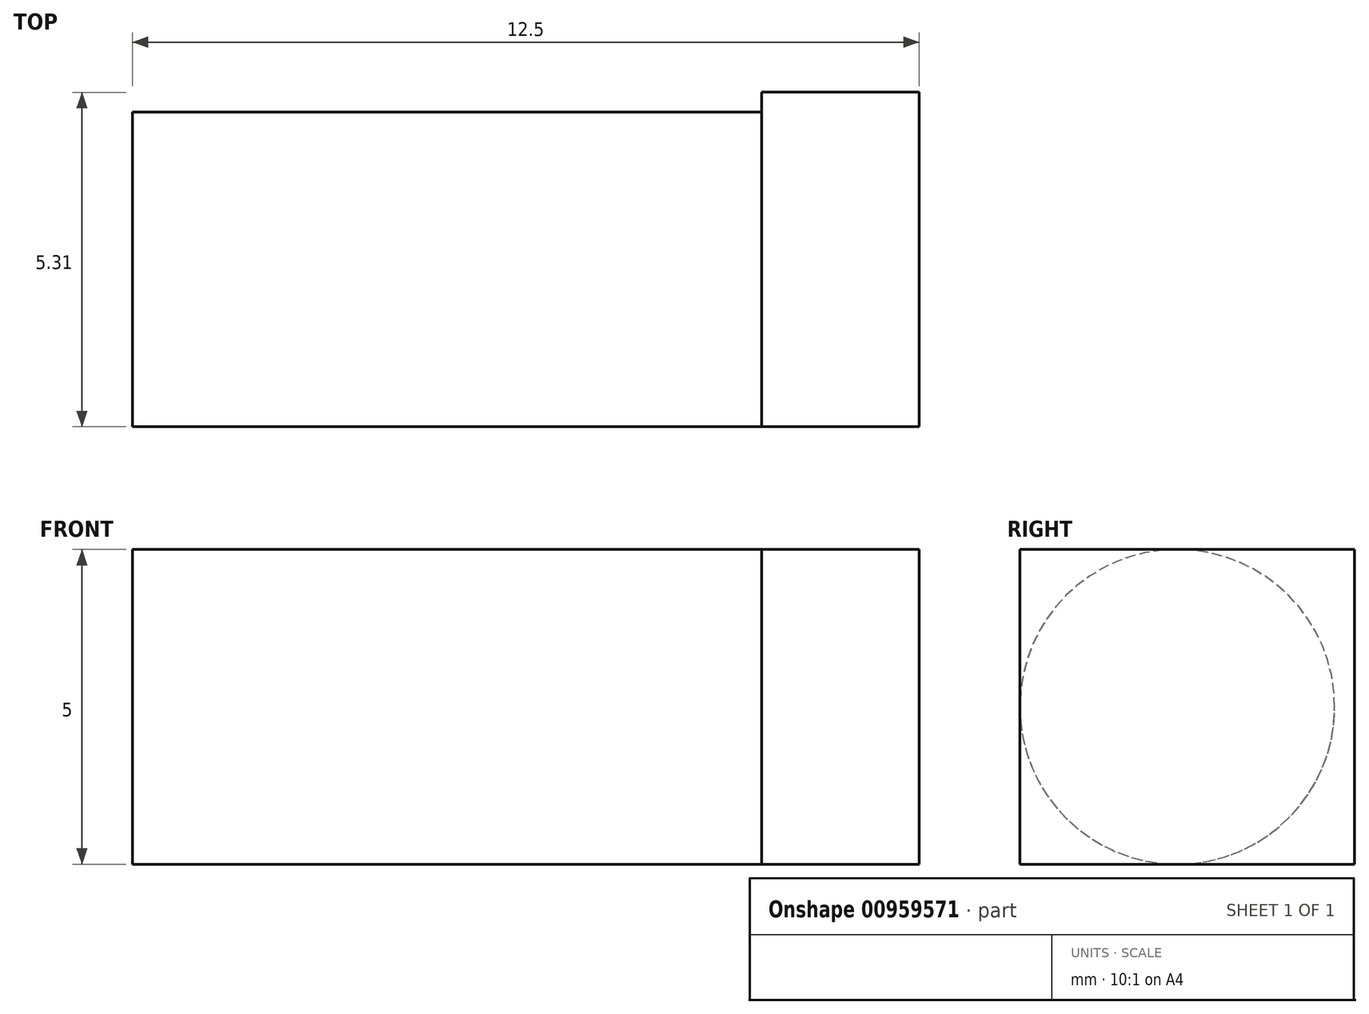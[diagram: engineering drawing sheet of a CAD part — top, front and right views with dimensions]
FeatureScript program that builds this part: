
annotation { "Feature Type Name" : "Feature", "Feature Type Description" : "" }
export const myFeature = defineFeature(function(context is Context, id is Id, definition is map)
    precondition{}
    {
        {
            var Q0;
            Q0=qCreatedBy(makeId("Right.planeOp"),FACE);
            var sketch = newSketch(context, id + "F0", { "sketchPlane" : qUnion([Q0])});
            skCircle(sketch, "E0", {"center": v(0, 0) * mm, "radius": 2.5 * mm});
            skSolve(sketch);
        }
        {
            var Q0;
            Q0=makeQuery(id+"F0.imprint","IMPRINT",FACE,{"disambiguationData":[TD([[makeQuery(id+"F0.imprint","IMPRINT",EDGE,{"derivedFrom":sQuery(id+"F0.wireOp",EDGE,"E0")}),1.0]])]});
            extrude(context, id + "F1", {"entities" : qUnion([Q0]), "depth" : 10 * mm, "offsetDistance" : 25 * mm});
        }
        {
            var Q0;
            Q0=makeQuery(id+"F1.opExtrude","CAP_FACE",FACE,{"disambiguationData":[OSD([sQuery(id+"F0.wireOp",EDGE,"E0")])],"isStart":false});
            var sketch = newSketch(context, id + "F2", { "sketchPlane" : qUnion([Q0])});
            skLineSegment(sketch, "E1", {"start": v(-2.5, 0) * mm, "end": v(-2.5, 2.5) * mm});
            skLineSegment(sketch, "E2.bottom", {"start": v(-2.5, 2.5) * mm, "end": v(2.81, 2.5) * mm});
            skLineSegment(sketch, "E2.top", {"start": v(-2.5, -2.5) * mm, "end": v(2.81, -2.5) * mm});
            skLineSegment(sketch, "E2.left", {"start": v(-2.5, 2.5) * mm, "end": v(-2.5, -2.5) * mm});
            skLineSegment(sketch, "E2.right", {"start": v(2.81, 2.5) * mm, "end": v(2.81, -2.5) * mm});
            skPoint(sketch, "E2.middle", {"position": v(0.16, 0) * mm});
            skPoint(sketch, "E3.start.orphan", {"position": v(0, 0) * mm});
            skSolve(sketch);
        }
        {
            var Q0;
            {var subQ0=makeQuery(id+"F1.opExtrude","CAP_EDGE",EDGE,{"disambiguationData":[OSD([sQuery(id+"F0.wireOp",EDGE,"E0")])],"isStart":false});var subQ1=makeQuery(id+"F2.imprint","INTERSECT",VERTEX,{"derivedFrom":[subQ0,sQuery(id+"F2.wireOp",EDGE,"E2.bottom")]});Q0=makeQuery(id+"F2.imprint","IMPRINT",FACE,{"disambiguationData":[TD([[makeQuery(id+"F2.imprint","IMPRINT",EDGE,{"disambiguationData":[TD([[subQ1,1.0]])],"derivedFrom":subQ0}),1.0]])]});}
            var Q1;
            {var subQ0=sQuery(id+"F2.wireOp",EDGE,"E2.left");var subQ1=sQuery(id+"F2.wireOp",EDGE,"E2.bottom");var subQ2=makeQuery(id+"F2.imprint","INTERSECT",VERTEX,{"derivedFrom":[subQ1,subQ0]});Q1=makeQuery(id+"F2.imprint","IMPRINT",FACE,{"disambiguationData":[TD([[makeQuery(id+"F2.imprint","IMPRINT",EDGE,{"disambiguationData":[TD([[subQ2,-1.0]])],"derivedFrom":subQ1}),-1.0]])]});}
            var Q2;
            {var subQ0=sQuery(id+"F2.wireOp",EDGE,"E2.right");Q2=makeQuery(id+"F2.imprint","IMPRINT",FACE,{"disambiguationData":[TD([[makeQuery(id+"F2.imprint","IMPRINT",EDGE,{"derivedFrom":subQ0}),-1.0]])]});}
            var Q3;
            {var subQ0=sQuery(id+"F2.wireOp",EDGE,"E2.left");var subQ1=sQuery(id+"F2.wireOp",EDGE,"E2.top");var subQ2=makeQuery(id+"F2.imprint","INTERSECT",VERTEX,{"derivedFrom":[subQ1,subQ0]});Q3=makeQuery(id+"F2.imprint","IMPRINT",FACE,{"disambiguationData":[TD([[makeQuery(id+"F2.imprint","IMPRINT",EDGE,{"disambiguationData":[TD([[subQ2,-1.0]])],"derivedFrom":subQ1}),1.0]])]});}
            extrude(context, id + "F3", {"entities" : qUnion([Q0, Q1, Q2, Q3]), "operationType" : NewBodyOperationType.ADD, "depth" : 2.5 * mm, "offsetDistance" : 25 * mm});
        }
    });
